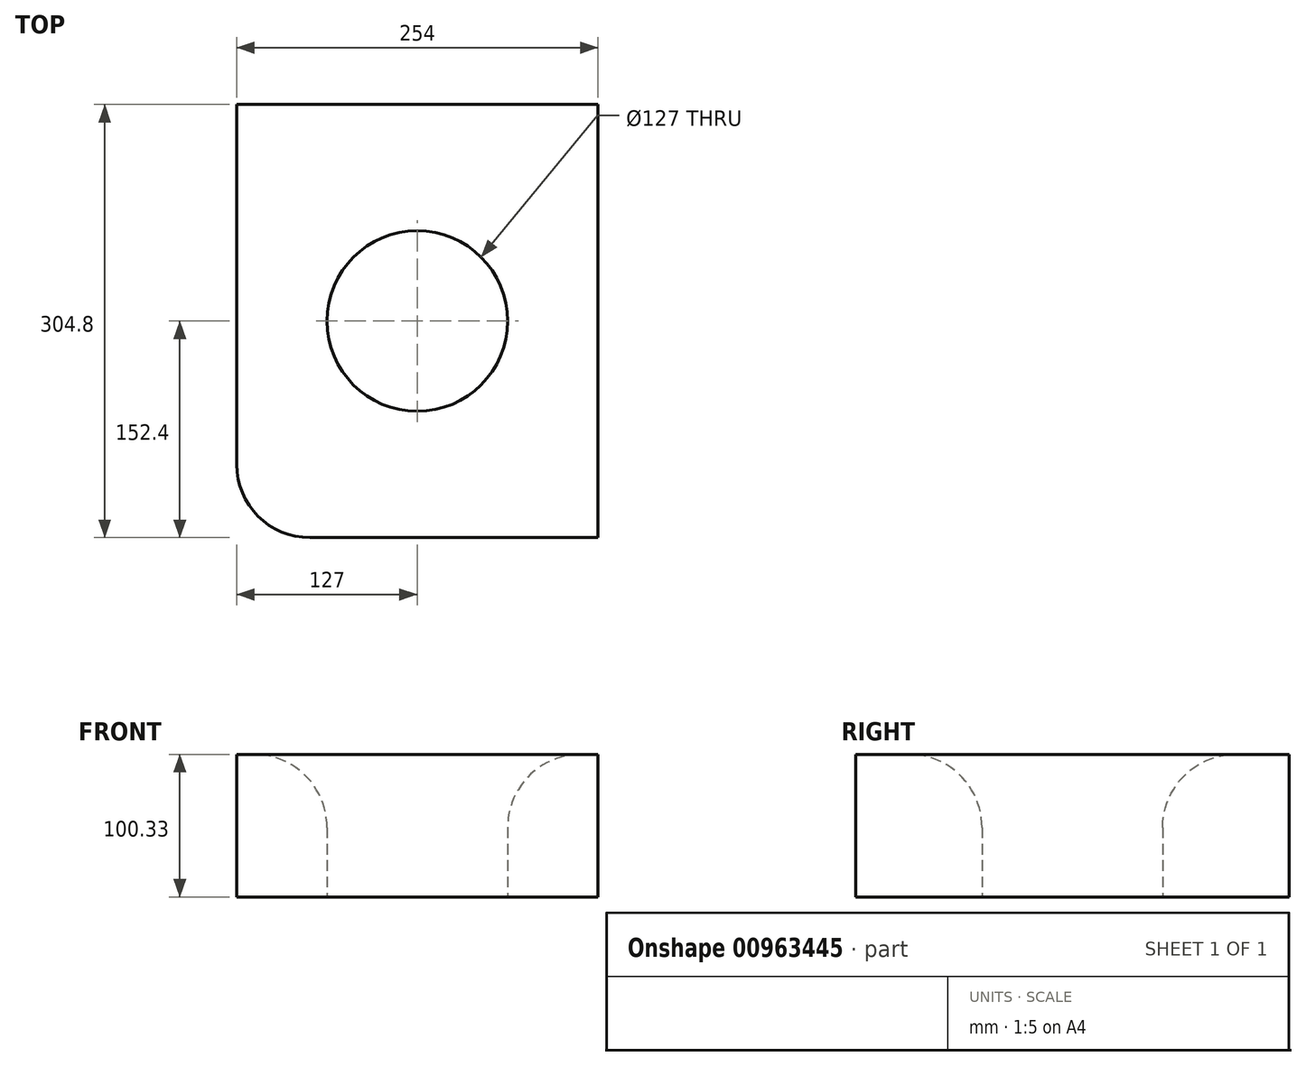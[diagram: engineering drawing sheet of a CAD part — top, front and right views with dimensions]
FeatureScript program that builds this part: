
annotation { "Feature Type Name" : "Feature", "Feature Type Description" : "" }
export const myFeature = defineFeature(function(context is Context, id is Id, definition is map)
    precondition{}
    {
        {
            var Q0;
            Q0=qCreatedBy(makeId("Top.planeOp"),FACE);
            var sketch = newSketch(context, id + "F0", { "sketchPlane" : qUnion([Q0])});
            skLineSegment(sketch, "E0.bottom", {"start": v(127, 152.4) * mm, "end": v(-127, 152.4) * mm});
            skLineSegment(sketch, "E0.top", {"start": v(127, -152.4) * mm, "end": v(-127, -152.4) * mm});
            skLineSegment(sketch, "E0.left", {"start": v(127, 152.4) * mm, "end": v(127, -152.4) * mm});
            skLineSegment(sketch, "E0.right", {"start": v(-127, 152.4) * mm, "end": v(-127, -152.4) * mm});
            skPoint(sketch, "E0.middle", {"position": v(0, 0) * mm});
            skCircle(sketch, "E1", {"center": v(0, 0) * mm, "radius": 63.5 * mm});
            skSolve(sketch);
        }
        {
            var Q0;
            Q0=makeQuery(id+"F0.imprint","IMPRINT",FACE,{"disambiguationData":[TD([[makeQuery(id+"F0.imprint","IMPRINT",EDGE,{"derivedFrom":sQuery(id+"F0.wireOp",EDGE,"E0.bottom")}),1.0]])]});
            extrude(context, id + "F1", {"entities" : qUnion([Q0]), "depth" : 100.33 * mm, "offsetDistance" : 25.4 * mm});
        }
        {
            var Q0;
            Q0=makeQuery(id+"F1.opExtrude","SWEPT_EDGE",EDGE,{"disambiguationData":[OSD([sQuery(id+"F0.wireOp",EDGE,"E0.top"),sQuery(id+"F0.wireOp",EDGE,"E0.right")])]});
            var Q1;
            Q1=makeQuery(id+"F1.opExtrude","CAP_EDGE",EDGE,{"disambiguationData":[OSD([sQuery(id+"F0.wireOp",EDGE,"E1")])],"isStart":false});
            fillet(context, id + "F2", {"entities" : qUnion([Q0, Q1]), "radius" : 51.5 * mm, "tangentPropagation" : true, "allowEdgeOverflow" : false});
        }
    });
